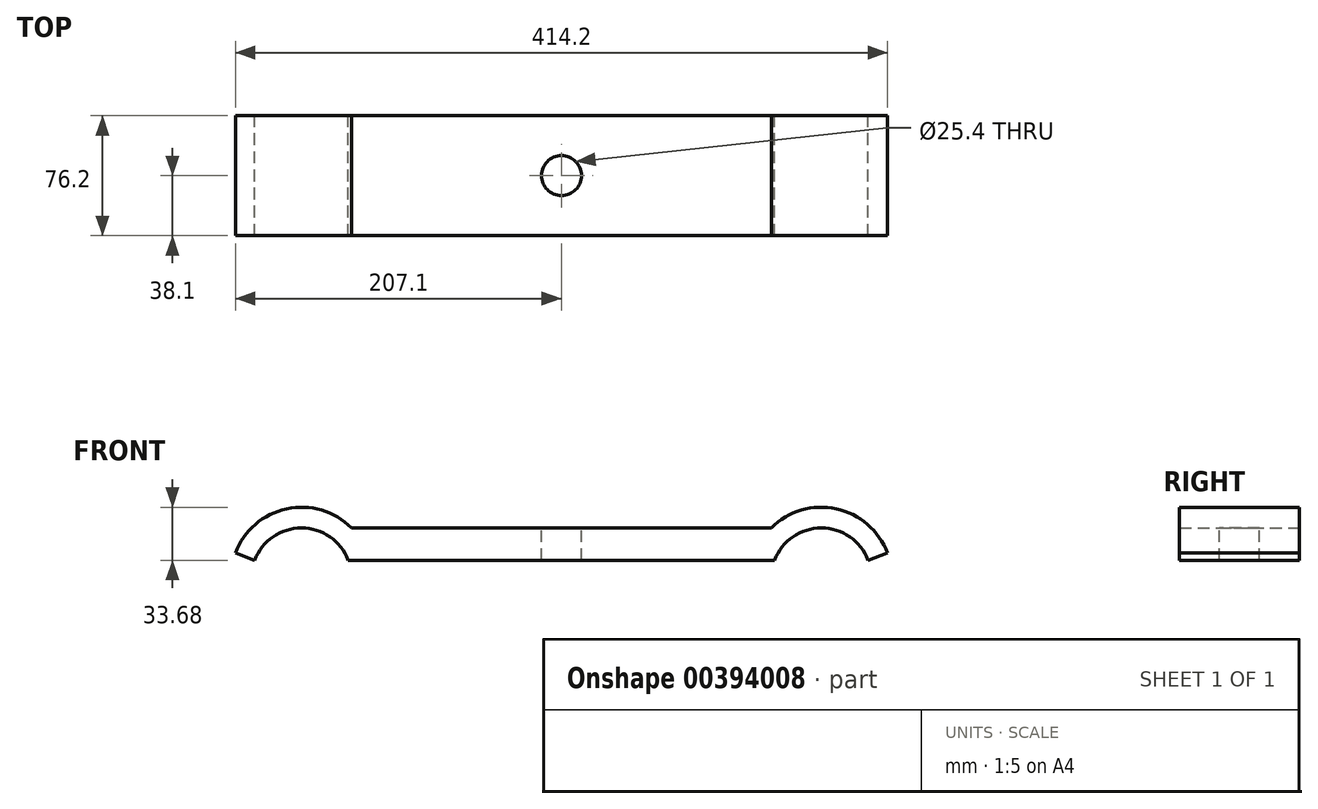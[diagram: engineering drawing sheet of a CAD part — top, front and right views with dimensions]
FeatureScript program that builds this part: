
annotation { "Feature Type Name" : "Feature", "Feature Type Description" : "" }
export const myFeature = defineFeature(function(context is Context, id is Id, definition is map)
    precondition{}
    {
        {
            var Q0;
            Q0=qCreatedBy(makeId("Front.planeOp"),FACE);
            var sketch = newSketch(context, id + "F0", { "sketchPlane" : qUnion([Q0])});
            skLineSegment(sketch, "E0.bottom", {"start": v(133.35, 15.87) * mm, "end": v(-133.35, 15.87) * mm});
            skPoint(sketch, "E0.middle", {"position": v(0, 0) * mm});
            skArc(sketch, "E1", {"start": v(-135.4, -4.65) * mm, "mid": v(-165.1, 15.87) * mm, "end": v(-194.8, -4.65) * mm});
            skArc(sketch, "E2", {"start": v(-133.35, 15.87) * mm, "mid": v(-174.55, 28.02) * mm, "end": v(-207.1, 0) * mm});
            skLineSegment(sketch, "E3", {"start": v(-194.8, -4.65) * mm, "end": v(-207.1, 0) * mm});
            skLineSegment(sketch, "E4", {"start": v(0, -4.65) * mm, "end": v(0, 0) * mm, "construction": true});
            skArc(sketch, "E5.MirrorCS", {"start": v(135.4, -4.65) * mm, "mid": v(165.1, 15.87) * mm, "end": v(194.8, -4.65) * mm});
            skLineSegment(sketch, "E6.MirrorCS", {"start": v(194.8, -4.65) * mm, "end": v(207.1, 0) * mm});
            skArc(sketch, "E7.MirrorCS", {"start": v(133.35, 15.87) * mm, "mid": v(174.55, 28.02) * mm, "end": v(207.1, 0) * mm});
            skLineSegment(sketch, "E8", {"start": v(-135.4, -4.65) * mm, "end": v(135.4, -4.65) * mm});
            skPoint(sketch, "E9.orphan", {"position": v(-133.35, -15.88) * mm});
            skPoint(sketch, "E0.top.end.orphan", {"position": v(0, -15.88) * mm});
            skPoint(sketch, "E0.top.start.orphan", {"position": v(133.35, -15.88) * mm});
            skSolve(sketch);
        }
        {
            var Q0;
            Q0=qSketchRegion(id+"F0",true);
            extrude(context, id + "F1", {"entities" : qUnion([Q0]), "depth" : 76.2 * mm});
        }
        {
            var Q0;
            Q0=makeQuery(id+"F1.opExtrude","SWEPT_FACE",FACE,{"disambiguationData":[OSD([sQuery(id+"F0.wireOp",EDGE,"E0.bottom")])]});
            var sketch = newSketch(context, id + "F2", { "sketchPlane" : qUnion([Q0])});
            skLineSegment(sketch, "E10", {"start": v(0, 0) * mm, "end": v(0, -76.2) * mm, "construction": true});
            skLineSegment(sketch, "E11", {"start": v(-133.35, -38.1) * mm, "end": v(133.35, -38.1) * mm, "construction": true});
            skCircle(sketch, "E12", {"center": v(0, -38.1) * mm, "radius": 12.7 * mm});
            skSolve(sketch);
        }
        {
            var Q0;
            Q0=makeQuery(id+"F2.imprint","IMPRINT",FACE,{"disambiguationData":[TD([[makeQuery(id+"F2.imprint","IMPRINT",EDGE,{"derivedFrom":sQuery(id+"F2.wireOp",EDGE,"E12")}),1.0]])]});
            extrude(context, id + "F3", {"entities" : qUnion([Q0]), "operationType" : NewBodyOperationType.REMOVE, "endBound" : BoundingType.UP_TO_NEXT, "oppositeDirection" : true, "depth" : 25.4 * mm});
        }
    });
